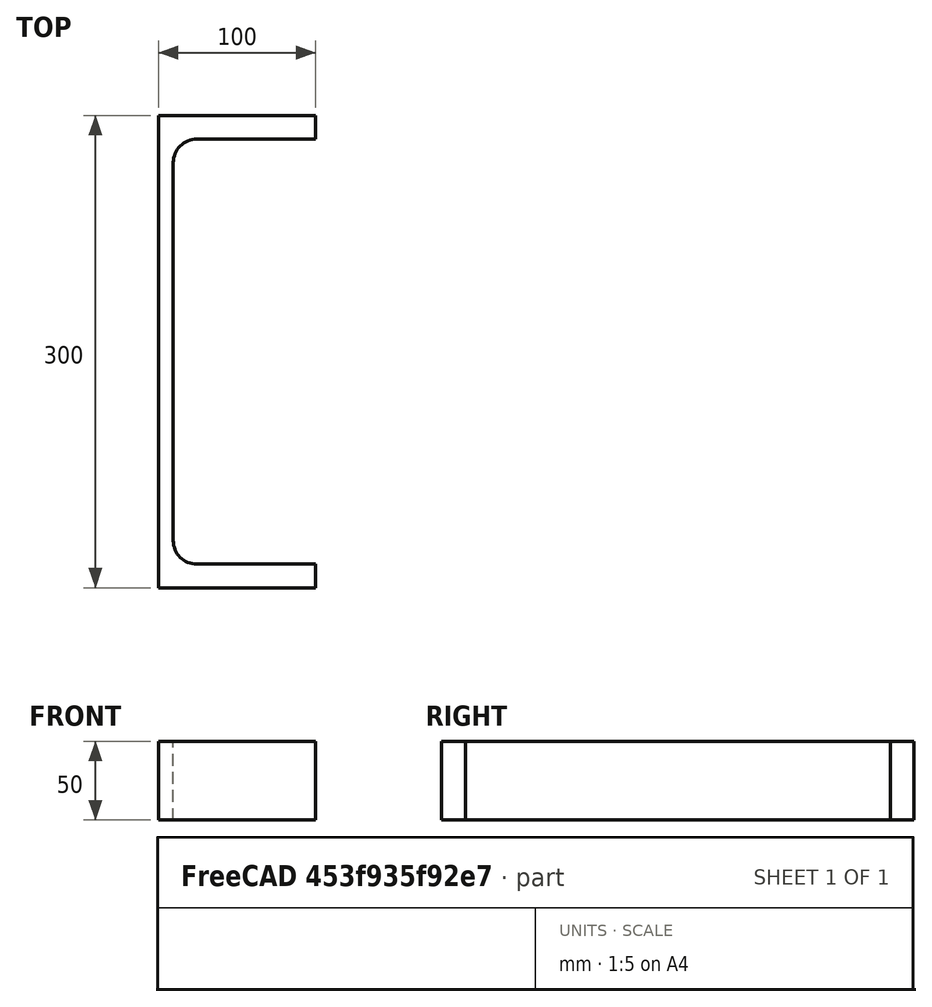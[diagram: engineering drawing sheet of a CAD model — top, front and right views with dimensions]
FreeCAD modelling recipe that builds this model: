
FCSTD DOCUMENT  (FreeCAD 0.20R29410 (Git))
Label: UPE-Profile 300 DIN1026-2 S235JR
License: All rights reserved
LicenseURL: http://en.wikipedia.org/wiki/All_rights_reserved
objects: Sketcher::SketchObject×1, Part::Extrusion×1
note: 2 computed .brp shape members not serialized (recipe doc carries the construction recipe); baked Part::Feature solids carry a one-line shape summary decoded from their .brp

FEATURE [Sketcher::SketchObject] Sketch
  FullyConstrained = true
  MapMode = 5
  sketch-geometry (10):
    g0: LineSegment StartX=9.5 StartY=-120 StartZ=0 EndX=9.5 EndY=120 EndZ=0
    g1: LineSegment StartX=24.5 StartY=135 StartZ=0 EndX=100 EndY=135 EndZ=0
    g2: LineSegment StartX=100 StartY=135 StartZ=0 EndX=100 EndY=150 EndZ=0
    g3: LineSegment StartX=100 StartY=-150 StartZ=0 EndX=100 EndY=-135 EndZ=0
    g4: LineSegment StartX=100 StartY=-135 StartZ=0 EndX=24.5 EndY=-135 EndZ=0
    g5: ArcOfCircle CenterX=24.5 CenterY=120 CenterZ=0 NormalX=0 NormalY=0 NormalZ=1 AngleXU=0 Radius=15 StartAngle=1.5708 EndAngle=3.14159
    g6: ArcOfCircle CenterX=24.5 CenterY=-120 CenterZ=0 NormalX=0 NormalY=0 NormalZ=1 AngleXU=0 Radius=15 StartAngle=3.14159 EndAngle=4.71239
    g7: LineSegment StartX=100 StartY=-150 StartZ=0 EndX=0 EndY=-150 EndZ=0
    g8: LineSegment StartX=0 StartY=-150 StartZ=0 EndX=0 EndY=150 EndZ=0
    g9: LineSegment StartX=0 StartY=150 StartZ=0 EndX=100 EndY=150 EndZ=0
  constraints (27):
    c: Vertical(g0)
    c: Coincident(g2,g1)
    c: Vertical(g2)
    c: Vertical(g3)
    c: Coincident(g4,g3)
    c: Horizontal(g4)
    c: Tangent(g1,g5) = 1.5708
    c: Tangent(g0,g5) = 1.5708
    c: Tangent(g0,g6) = 1.5708
    c: Tangent(g4,g6) = 1.5708
    c: Symmetric(g2,g3,g-1)
    c: DistanceY(g2) = 15
    c: Radius(g5) = 15
    c: Coincident(g3,g7)
    c: PointOnObject(g7,g-2)
    c: Horizontal(g7)
    c: Coincident(g7,g8)
    c: PointOnObject(g8,g-2)
    c: Coincident(g8,g9)
    c: Coincident(g9,g2)
    c: Horizontal(g9)
    c: Distance(g-1,g0) = 9.5
    c: DistanceX(g9,g9) = 100
    c: Horizontal(g1)
    c: Equal(g3,g2)
    c: Equal(g5,g6)
    c: DistanceY(g3,g2) = 300
FEATURE [Part::Extrusion] Extrude  label="UPE-Profile 300 DIN1026-2 S235JR"
  Base = -> Sketch
  Dir = (0,0,50)
  DirMode = 0
  FaceMakerClass = Part::FaceMakerExtrusion
  LengthFwd = 0
  LengthRev = 0
  Solid = true
  Symmetric = false
